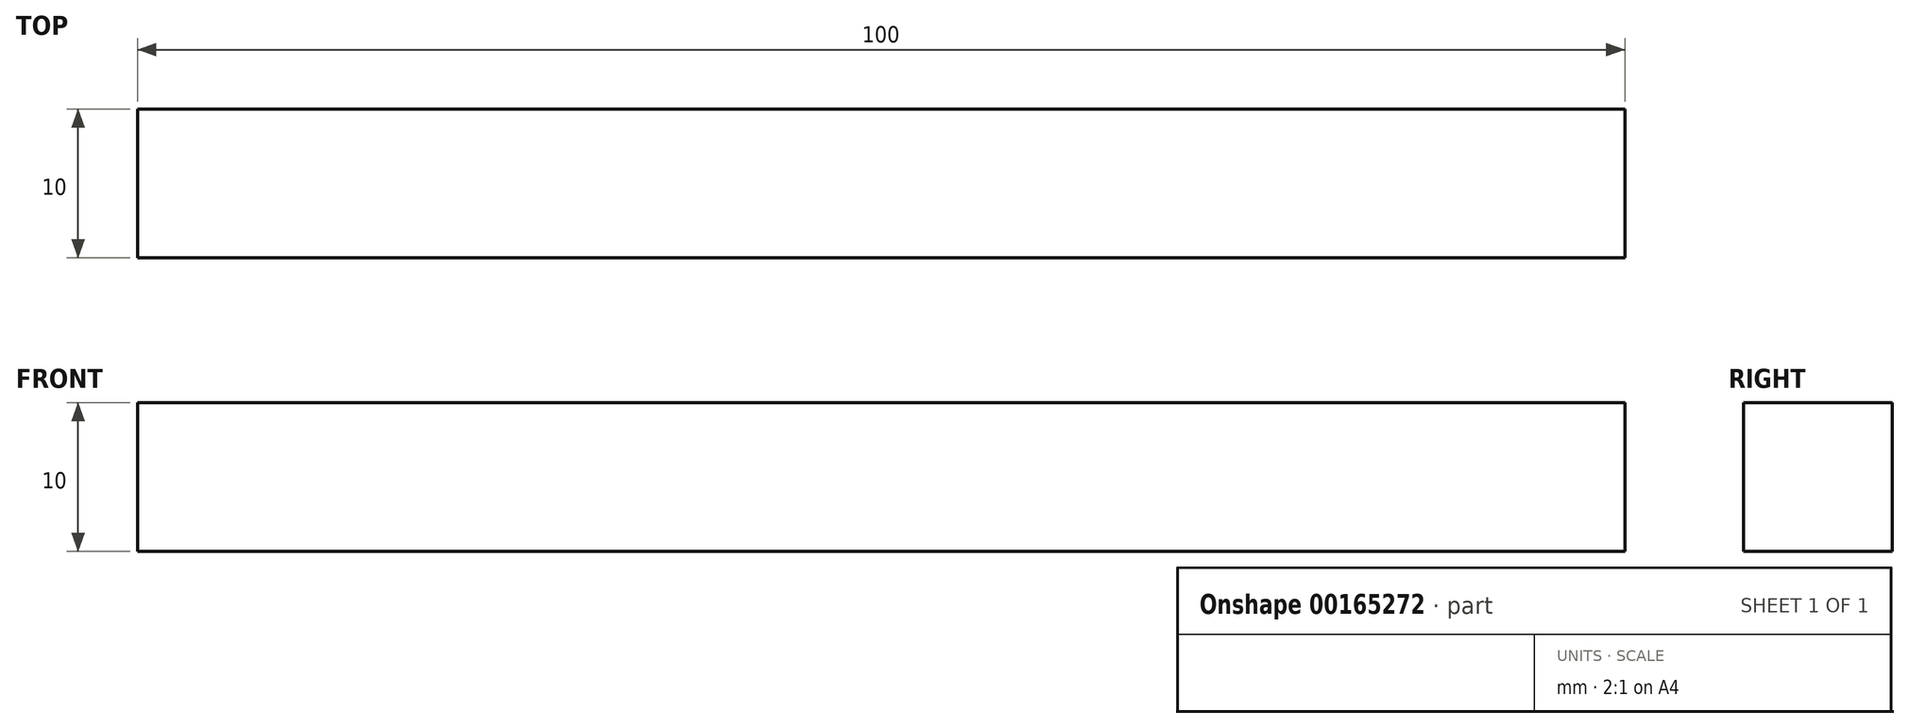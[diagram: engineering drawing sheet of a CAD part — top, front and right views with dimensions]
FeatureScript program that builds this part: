
annotation { "Feature Type Name" : "Feature", "Feature Type Description" : "" }
export const myFeature = defineFeature(function(context is Context, id is Id, definition is map)
    precondition{}
    {
        {
            var Q0;
            Q0=qCreatedBy(makeId("Top.planeOp"),FACE);
            var sketch = newSketch(context, id + "F0", { "sketchPlane" : qUnion([Q0])});
            skLineSegment(sketch, "E0.bottom", {"start": v(-67.78, -14.12) * mm, "end": v(32.22, -14.12) * mm});
            skLineSegment(sketch, "E0.top", {"start": v(-67.78, -24.12) * mm, "end": v(32.22, -24.12) * mm});
            skLineSegment(sketch, "E0.left", {"start": v(-67.78, -14.12) * mm, "end": v(-67.78, -24.12) * mm});
            skLineSegment(sketch, "E0.right", {"start": v(32.22, -14.12) * mm, "end": v(32.22, -24.12) * mm});
            skLineSegment(sketch, "E1.bottom", {"start": v(-67.78, -14.12) * mm, "end": v(-57.78, -14.12) * mm});
            skLineSegment(sketch, "E1.top", {"start": v(-67.78, 75.88) * mm, "end": v(-57.78, 75.88) * mm});
            skLineSegment(sketch, "E1.left", {"start": v(-67.78, -14.12) * mm, "end": v(-67.78, 75.88) * mm});
            skLineSegment(sketch, "E1.right", {"start": v(-57.78, -14.12) * mm, "end": v(-57.78, 75.88) * mm});
            skSolve(sketch);
        }
        {
            var Q0;
            Q0=makeQuery(id+"F0.imprint","IMPRINT",FACE,{"disambiguationData":[TD([[makeQuery(id+"F0.imprint","IMPRINT",EDGE,{"derivedFrom":sQuery(id+"F0.wireOp",EDGE,"E1.bottom")}),1.0]])]});
            var Q1;
            Q1=makeQuery(id+"F0.imprint","IMPRINT",FACE,{"disambiguationData":[TD([[makeQuery(id+"F0.imprint","IMPRINT",EDGE,{"derivedFrom":sQuery(id+"F0.wireOp",EDGE,"E0.bottom")}),-1.0]])]});
            extrude(context, id + "F1", {"entities" : qUnion([Q0, Q1]), "depth" : 10 * mm});
        }
    });
